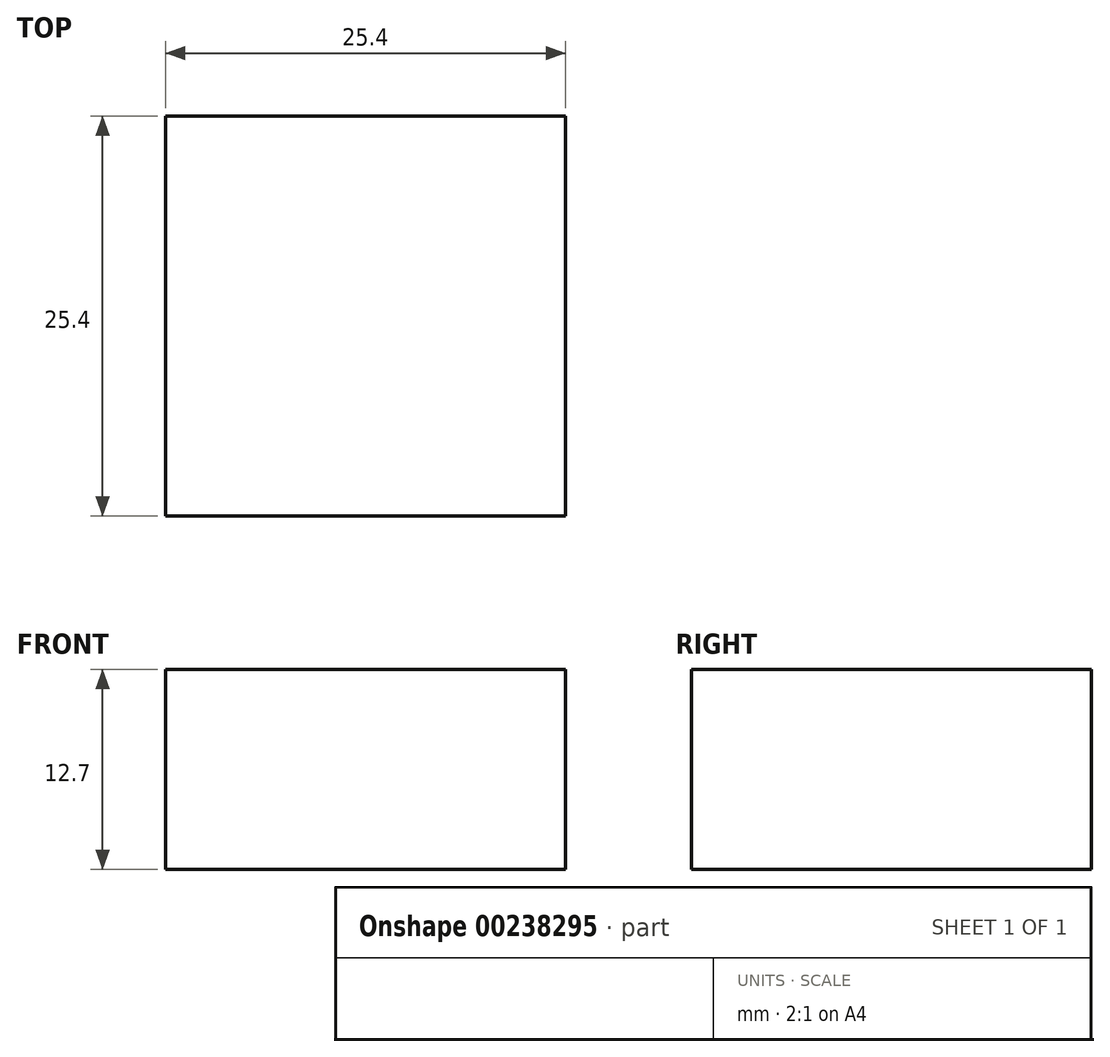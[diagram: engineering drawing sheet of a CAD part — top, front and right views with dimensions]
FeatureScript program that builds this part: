
annotation { "Feature Type Name" : "Feature", "Feature Type Description" : "" }
export const myFeature = defineFeature(function(context is Context, id is Id, definition is map)
    precondition{}
    {
        {
            var Q0;
            Q0=qCreatedBy(makeId("Top.planeOp"),FACE);
            var sketch = newSketch(context, id + "F0", { "sketchPlane" : qUnion([Q0])});
            skLineSegment(sketch, "E0.bottom", {"start": v(0, 0) * mm, "end": v(25.4, 0) * mm});
            skLineSegment(sketch, "E0.top", {"start": v(0, 25.4) * mm, "end": v(25.4, 25.4) * mm});
            skLineSegment(sketch, "E0.left", {"start": v(0, 0) * mm, "end": v(0, 25.4) * mm});
            skLineSegment(sketch, "E0.right", {"start": v(25.4, 0) * mm, "end": v(25.4, 25.4) * mm});
            skSolve(sketch);
        }
        {
            var Q0;
            Q0 = qSketchRegion(id + "F0", true);
            extrude(context, id + "F1", {"entities" : qUnion([Q0]), "depth" : 12.7 * mm});
        }
    });
